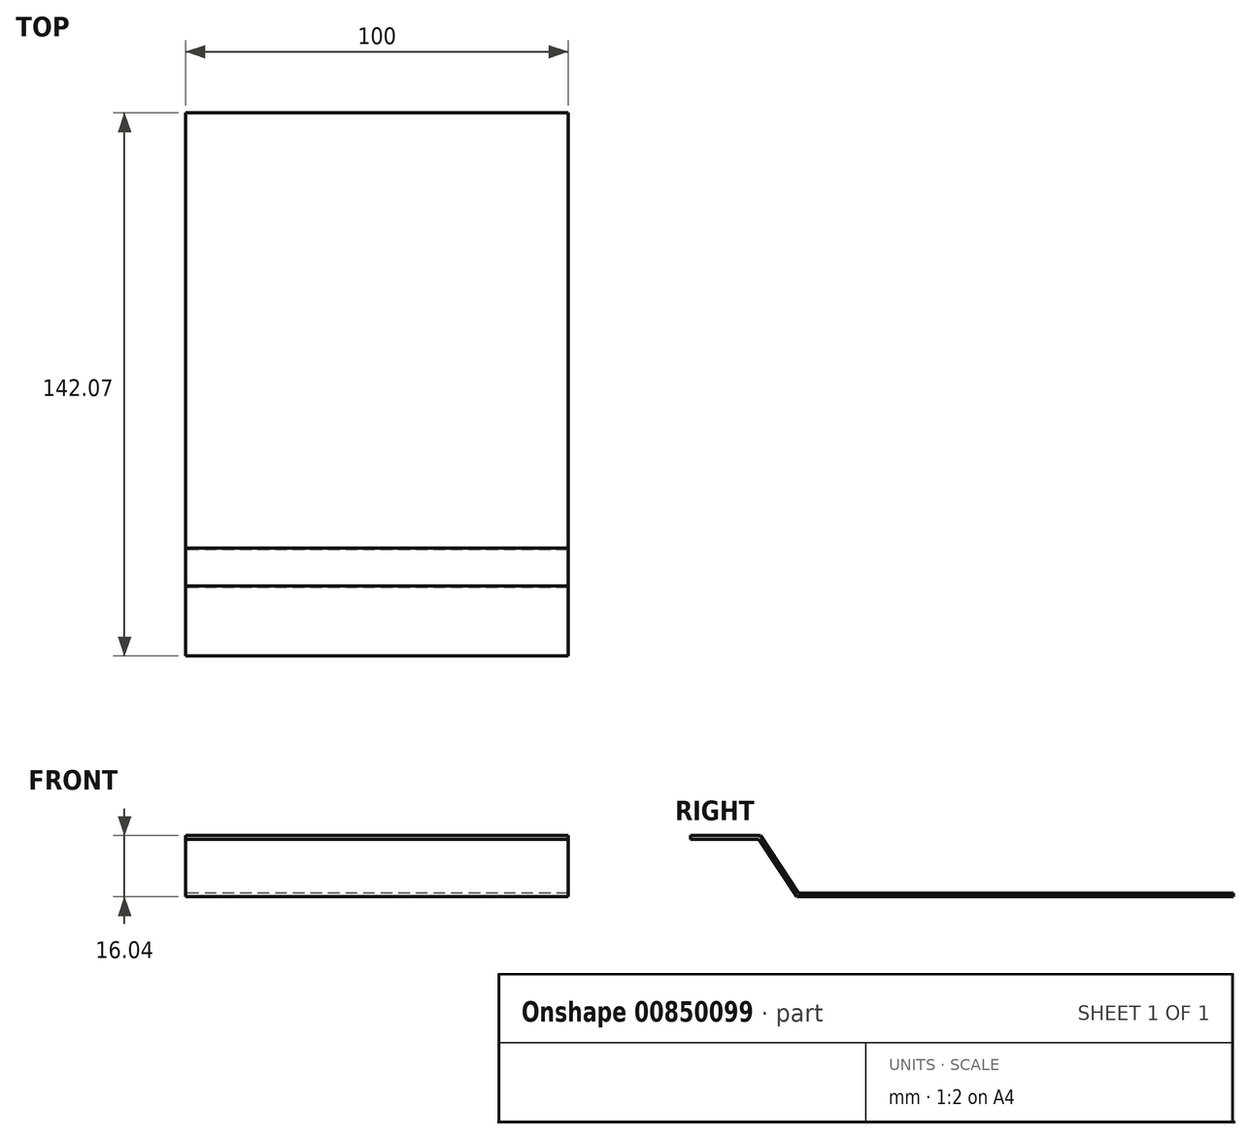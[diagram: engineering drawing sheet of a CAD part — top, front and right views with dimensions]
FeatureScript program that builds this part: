
annotation { "Feature Type Name" : "Feature", "Feature Type Description" : "" }
export const myFeature = defineFeature(function(context is Context, id is Id, definition is map)
    precondition{}
    {
        {
            var Q0;
            Q0=qCreatedBy(makeId("Right.planeOp"),FACE);
            var sketch = newSketch(context, id + "F0", { "sketchPlane" : qUnion([Q0])});
            skLineSegment(sketch, "E0.bottom", {"start": v(-38.85, 0.5) * mm, "end": v(75, 0.5) * mm});
            skLineSegment(sketch, "E0.top", {"start": v(-39.19, -0.5) * mm, "end": v(75, -0.5) * mm});
            skLineSegment(sketch, "E0.right", {"start": v(75, 0.5) * mm, "end": v(75, -0.5) * mm});
            skPoint(sketch, "E0.middle", {"position": v(0, 0) * mm});
            skLineSegment(sketch, "E1", {"start": v(-39.85, 0.5) * mm, "end": v(-49.1, 14.54) * mm});
            skLineSegment(sketch, "E2", {"start": v(-49.1, 14.54) * mm, "end": v(-67.07, 14.54) * mm});
            skLineSegment(sketch, "E3", {"start": v(-67.07, 14.54) * mm, "end": v(-67.07, 15.54) * mm});
            skLineSegment(sketch, "E4", {"start": v(-38.85, 0.5) * mm, "end": v(-48.76, 15.54) * mm});
            skLineSegment(sketch, "E5", {"start": v(-67.07, 15.54) * mm, "end": v(-48.76, 15.54) * mm});
            skLineSegment(sketch, "E6", {"start": v(-39.85, 0.5) * mm, "end": v(-39.19, -0.5) * mm});
            skPoint(sketch, "E0.left.end.orphan", {"position": v(-75, -0.5) * mm});
            skPoint(sketch, "E0.left.start.orphan", {"position": v(-75, 0.5) * mm});
            skSolve(sketch);
        }
        {
            var Q0;
            Q0=qSketchRegion(id+"F0",true);
            extrude(context, id + "F1", {"entities" : qUnion([Q0]), "depth" : 100 * mm, "offsetDistance" : 25 * mm});
        }
    });
